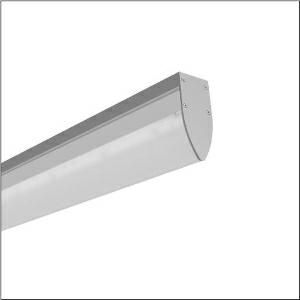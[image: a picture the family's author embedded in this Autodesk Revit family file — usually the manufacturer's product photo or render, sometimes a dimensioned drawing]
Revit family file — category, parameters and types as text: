
# Revit family: mira_r__21_td_51fr527p454a_1793
name_source: partatom
category: Lighting Fixtures
units: mm (PartAtom-declared; Revit-internal decimal feet)

## family parameters
Cut with Voids When Loaded = No
Host = Face
Light Source = No
Part Type = Normal
Room Calculation Point = No
Round Connector Dimension = Use Diameter
Shared = No

## types (1)
- Mira® 21 TD (1 x LED, 5040 lm, 34 W, 4000K)
    Apparent Load = 34 VA
    CIE Flux Codes = 40 68 87 81 100
    Color Rendering = 80
    Color Temperature = 4000K
    Default Elevation = 1800 mm
    Description = Mira® 21 TD, clean room luminaire, primary light control with reflector, primary optical cover: cover, of PMMA, frosted, light emission: direct distribution, primary light characteristic: symmetric, installation type: surface-mounted, LED, rated luminous flux: 5.040lm, luminous efficacy: 148lm/W, light colour: 840, colour temperature: 4000K, control gear: ECG, with terminal, 3-pole, max. 2.5mm², mains connection: 230V, AC, 50/60Hz, rated input power: 34W, luminaire housing, of sheet steel, coated, pure white, length: 1.500mm, width: 55mm, height: 120mm, protection rating (complete): IP43, insulation class (complete): insulation class I (protective earthing), certification: CE, UKCA, permissible operating ambient temperature: -5..+40°C, standard: EN 50419, packaging unit: 1 piece
    Height = 0 mm  [stored 0 ft]
    Lamp = 1 x LED
    Lamp Light Flux = 5040 lm
    Lamp Power = 34 W
    Lamp count = 1
    Length = 1500 mm
    Luminous efficacy = 148 lm/W
    Manufacturer = Siteco
    ModVariant = No
    Model = 51FR527P454A
    Mounting Place = Ceiling
    Mounting Type = Recessed
    Number of Poles = 1
    OnlyDefault = Yes
    Power Factor = 1
    Product Name = Mira® 21 TD
    Product group = clean room luminaire
    ProductGroupID = 401
    Protection Class = Protection class I
    Protection Degree = IP 43
    RLX_Detail_Level = 1
    RlxData = <blob elided: 25141 chars, md5=e6787f94>
    Socket = socket
    Standby Power = 0 W
    System Light Flux = 5040 lm
    System Power = 34 W
    Type Comments = Product without accessories
    Type Image = l_1007115.jpg
    URL = http://relux.com
    VarID = ---
    Voltage = 0 V
    Weight = 0.00 kg
    Width = 55 mm

note: [stored X ft] marks values corroborated as IEEE doubles in the binary element streams (Revit-internal decimal feet)

## geometry (parser evidence)
native form markers: Blend x4, Sweep x15
no freeform markers — native parametric forms only
